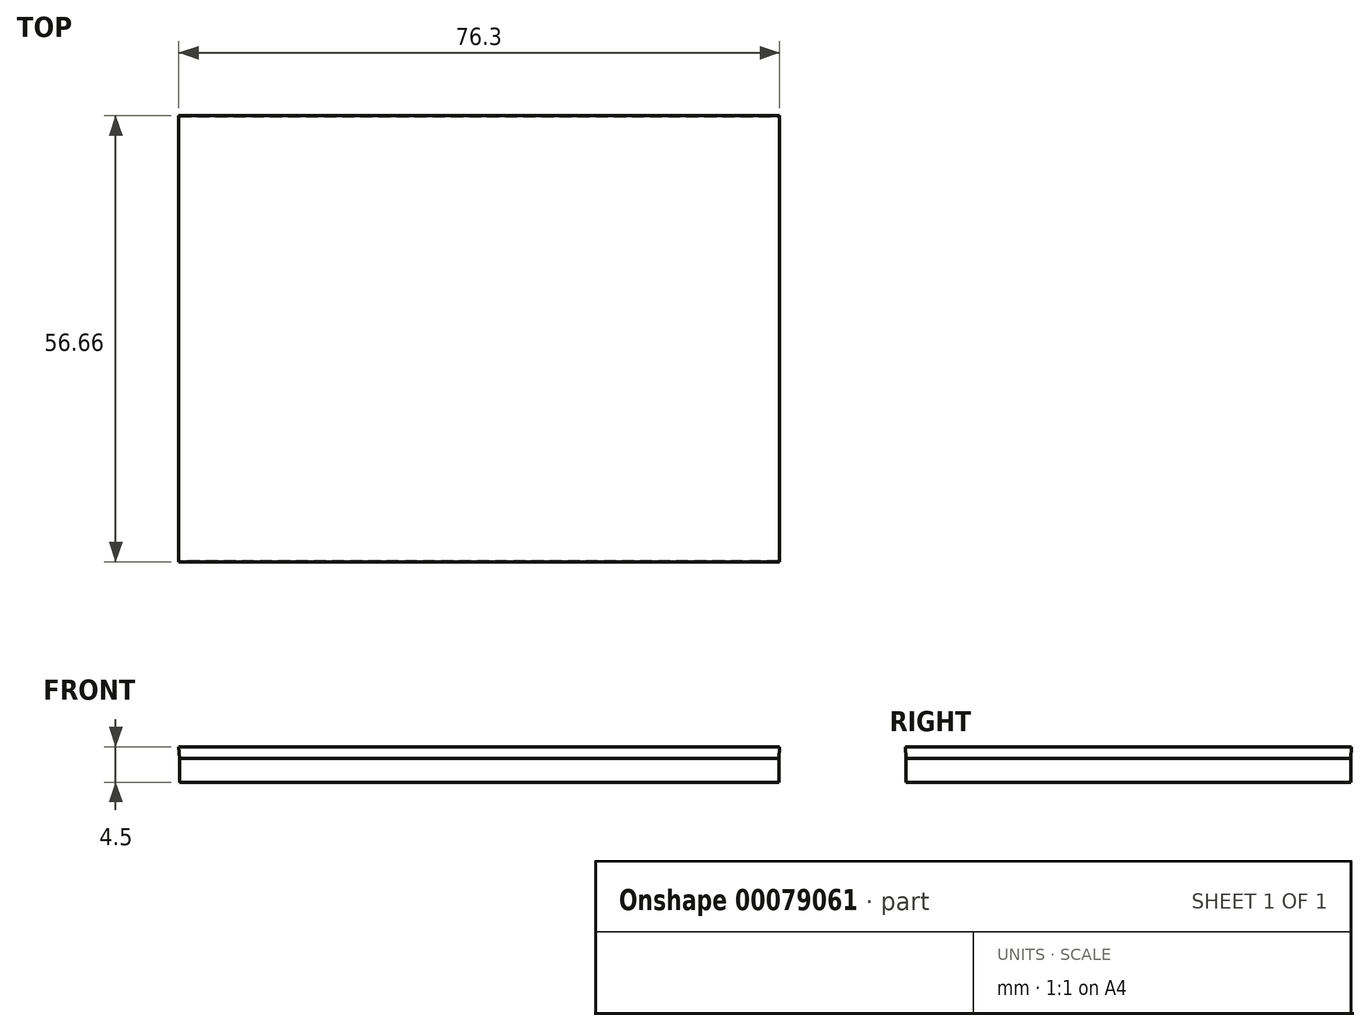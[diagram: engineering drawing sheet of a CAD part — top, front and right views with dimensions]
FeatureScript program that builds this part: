
annotation { "Feature Type Name" : "Feature", "Feature Type Description" : "" }
export const myFeature = defineFeature(function(context is Context, id is Id, definition is map)
    precondition{}
    {
        {
            var Q0;
            Q0=qCreatedBy(makeId("Top.planeOp"),FACE);
            var sketch = newSketch(context, id + "F0", { "sketchPlane" : qUnion([Q0])});
            skLineSegment(sketch, "E0.bottom", {"start": v(-76.14, 56.5) * mm, "end": v(0, 56.5) * mm});
            skLineSegment(sketch, "E0.top", {"start": v(-76.14, 0) * mm, "end": v(0, 0) * mm});
            skLineSegment(sketch, "E0.left", {"start": v(-76.14, 56.5) * mm, "end": v(-76.14, 0) * mm});
            skLineSegment(sketch, "E0.right", {"start": v(0, 56.5) * mm, "end": v(0, 0) * mm});
            skSolve(sketch);
        }
        {
            var Q0;
            Q0=qSketchRegion(id+"F0",true);
            extrude(context, id + "F1", {"entities" : qUnion([Q0]), "depth" : 3 * mm});
        }
        {
            var Q0;
            Q0=makeQuery(id+"F1.opExtrude","CAP_FACE",FACE,{"disambiguationData":[OSD([sQuery(id+"F0.wireOp",EDGE,"E0.bottom"),sQuery(id+"F0.wireOp",EDGE,"E0.top"),sQuery(id+"F0.wireOp",EDGE,"E0.left"),sQuery(id+"F0.wireOp",EDGE,"E0.right")])],"isStart":false});
            var sketch = newSketch(context, id + "F2", { "sketchPlane" : qUnion([Q0])});
            skLineSegment(sketch, "E1.bottom", {"start": v(-76.14, 56.5) * mm, "end": v(0, 56.5) * mm});
            skLineSegment(sketch, "E1.top", {"start": v(-76.14, 0) * mm, "end": v(0, 0) * mm});
            skLineSegment(sketch, "E1.left", {"start": v(-76.14, 56.5) * mm, "end": v(-76.14, 0) * mm});
            skLineSegment(sketch, "E1.right", {"start": v(0, 56.5) * mm, "end": v(0, 0) * mm});
            skSolve(sketch);
        }
        {
            var Q0;
            Q0=makeQuery(id+"F2.imprint","IMPRINT",FACE,{"disambiguationData":[TD([[makeQuery(id+"F2.imprint","IMPRINT",EDGE,{"derivedFrom":sQuery(id+"F2.wireOp",EDGE,"E1.bottom")}),-1.0]])]});
            extrude(context, id + "F3", {"entities" : qUnion([Q0]), "depth" : 1.5 * mm, "hasDraft" : true, "draftAngle" : 3 * degree});
        }
    });
